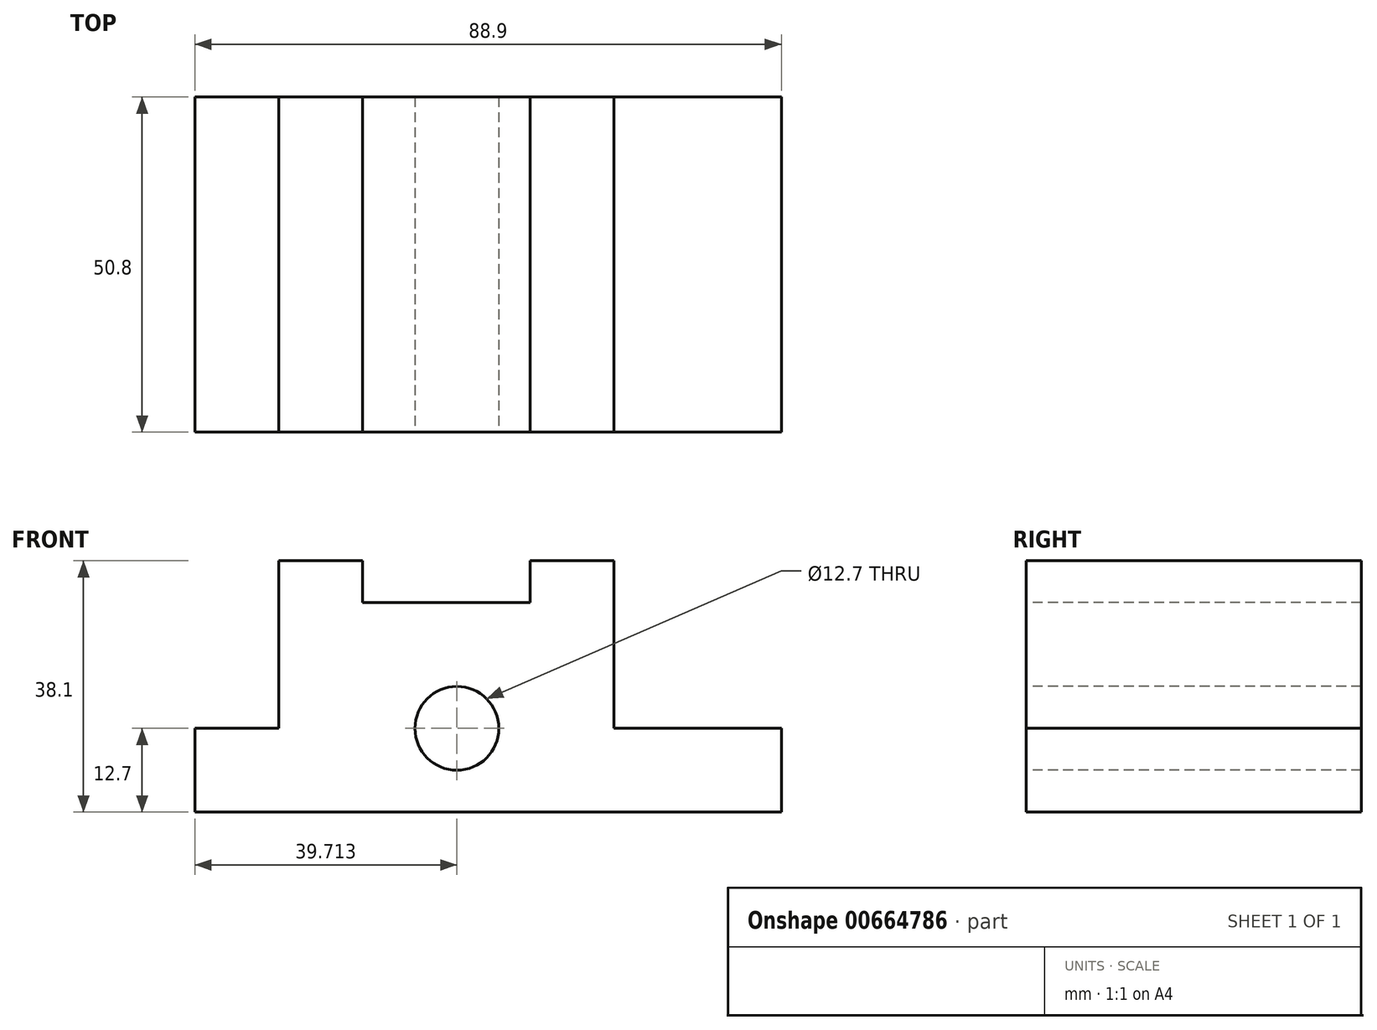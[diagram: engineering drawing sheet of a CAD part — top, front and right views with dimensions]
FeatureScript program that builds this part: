
annotation { "Feature Type Name" : "Feature", "Feature Type Description" : "" }
export const myFeature = defineFeature(function(context is Context, id is Id, definition is map)
    precondition{}
    {
        {
            var Q0;
            Q0=qCreatedBy(makeId("Front.planeOp"),FACE);
            var sketch = newSketch(context, id + "F0", { "sketchPlane" : qUnion([Q0])});
            skLineSegment(sketch, "E0.bottom", {"start": v(-44.45, 19.05) * mm, "end": v(44.45, 19.05) * mm});
            skLineSegment(sketch, "E0.top", {"start": v(-44.45, -19.05) * mm, "end": v(44.45, -19.05) * mm});
            skLineSegment(sketch, "E0.left", {"start": v(-44.45, 19.05) * mm, "end": v(-44.45, -19.05) * mm});
            skLineSegment(sketch, "E0.right", {"start": v(44.45, 19.05) * mm, "end": v(44.45, -19.05) * mm});
            skPoint(sketch, "E0.middle", {"position": v(0, 0) * mm});
            skSolve(sketch);
        }
        {
            var Q0;
            Q0=makeQuery(id+"F0.imprint","IMPRINT",FACE,{"disambiguationData":[TD([[makeQuery(id+"F0.imprint","IMPRINT",EDGE,{"derivedFrom":sQuery(id+"F0.wireOp",EDGE,"E0.bottom")}),-1.0]])]});
            extrude(context, id + "F1", {"entities" : qUnion([Q0]), "depth" : 50.8 * mm, "offsetDistance" : 25.4 * mm});
        }
        {
            var Q0;
            Q0=makeQuery(id+"F1.opExtrude","CAP_FACE",FACE,{"disambiguationData":[OSD([sQuery(id+"F0.wireOp",EDGE,"E0.bottom"),sQuery(id+"F0.wireOp",EDGE,"E0.top"),sQuery(id+"F0.wireOp",EDGE,"E0.left"),sQuery(id+"F0.wireOp",EDGE,"E0.right")])],"isStart":false});
            var sketch = newSketch(context, id + "F2", { "sketchPlane" : qUnion([Q0])});
            skLineSegment(sketch, "E1.bottom", {"start": v(-44.45, 19.05) * mm, "end": v(-31.75, 19.05) * mm});
            skLineSegment(sketch, "E1.top", {"start": v(-44.45, -6.35) * mm, "end": v(-31.75, -6.35) * mm});
            skLineSegment(sketch, "E1.left", {"start": v(-44.45, 19.05) * mm, "end": v(-44.45, -6.35) * mm});
            skLineSegment(sketch, "E1.right", {"start": v(-31.75, 19.05) * mm, "end": v(-31.75, -6.35) * mm});
            skSolve(sketch);
        }
        {
            var Q0;
            Q0=makeQuery(id+"F2.imprint","IMPRINT",FACE,{"disambiguationData":[TD([[makeQuery(id+"F2.imprint","IMPRINT",EDGE,{"derivedFrom":sQuery(id+"F2.wireOp",EDGE,"E1.bottom")}),-1.0]])]});
            extrude(context, id + "F3", {"entities" : qUnion([Q0]), "operationType" : NewBodyOperationType.REMOVE, "endBound" : BoundingType.THROUGH_ALL, "oppositeDirection" : true, "depth" : 25.4 * mm, "offsetDistance" : 25.4 * mm});
        }
        {
            var Q0;
            Q0=makeQuery(id+"F1.opExtrude","CAP_FACE",FACE,{"disambiguationData":[OSD([sQuery(id+"F0.wireOp",EDGE,"E0.bottom"),sQuery(id+"F0.wireOp",EDGE,"E0.top"),sQuery(id+"F0.wireOp",EDGE,"E0.left"),sQuery(id+"F0.wireOp",EDGE,"E0.right")])],"isStart":false});
            var sketch = newSketch(context, id + "F4", { "sketchPlane" : qUnion([Q0])});
            skLineSegment(sketch, "E2.bottom", {"start": v(44.45, 19.05) * mm, "end": v(19.05, 19.05) * mm});
            skLineSegment(sketch, "E2.top", {"start": v(44.45, -6.35) * mm, "end": v(19.05, -6.35) * mm});
            skLineSegment(sketch, "E2.left", {"start": v(44.45, 19.05) * mm, "end": v(44.45, -6.35) * mm});
            skLineSegment(sketch, "E2.right", {"start": v(19.05, 19.05) * mm, "end": v(19.05, -6.35) * mm});
            skSolve(sketch);
        }
        {
            var Q0;
            Q0=makeQuery(id+"F4.imprint","IMPRINT",FACE,{"disambiguationData":[TD([[makeQuery(id+"F4.imprint","IMPRINT",EDGE,{"derivedFrom":sQuery(id+"F4.wireOp",EDGE,"E2.bottom")}),-1.0]])]});
            extrude(context, id + "F5", {"entities" : qUnion([Q0]), "operationType" : NewBodyOperationType.REMOVE, "endBound" : BoundingType.THROUGH_ALL, "oppositeDirection" : true, "depth" : 25.4 * mm, "offsetDistance" : 25.4 * mm});
        }
        {
            var Q0;
            Q0=makeQuery(id+"F1.opExtrude","CAP_FACE",FACE,{"disambiguationData":[OSD([sQuery(id+"F0.wireOp",EDGE,"E0.bottom"),sQuery(id+"F0.wireOp",EDGE,"E0.top"),sQuery(id+"F0.wireOp",EDGE,"E0.left"),sQuery(id+"F0.wireOp",EDGE,"E0.right")])],"isStart":false});
            var sketch = newSketch(context, id + "F6", { "sketchPlane" : qUnion([Q0])});
            skCircle(sketch, "E3", {"center": v(-4.74, -6.35) * mm, "radius": 6.35 * mm});
            skSolve(sketch);
        }
        {
            var Q0;
            Q0=makeQuery(id+"F6.imprint","IMPRINT",FACE,{"disambiguationData":[TD([[makeQuery(id+"F6.imprint","IMPRINT",EDGE,{"derivedFrom":sQuery(id+"F6.wireOp",EDGE,"E3")}),1.0]])]});
            var Q1;
            Q1=sQuery(id+"F6.wireOp",EDGE,"E3");
            extrude(context, id + "F7", {"entities" : qUnion([Q0]), "operationType" : NewBodyOperationType.REMOVE, "surfaceEntities" : qUnion([Q1]), "endBound" : BoundingType.THROUGH_ALL, "oppositeDirection" : true, "depth" : 25.4 * mm, "offsetDistance" : 25.4 * mm});
        }
        {
            var Q0;
            Q0=makeQuery(id+"F1.opExtrude","SWEPT_FACE",FACE,{"disambiguationData":[OSD([sQuery(id+"F0.wireOp",EDGE,"E0.bottom")])]});
            var sketch = newSketch(context, id + "F8", { "sketchPlane" : qUnion([Q0])});
            skLineSegment(sketch, "E4.bottom", {"start": v(-19.05, 0) * mm, "end": v(6.35, 0) * mm});
            skLineSegment(sketch, "E4.top", {"start": v(-19.05, -50.8) * mm, "end": v(6.35, -50.8) * mm});
            skLineSegment(sketch, "E4.left", {"start": v(-19.05, 0) * mm, "end": v(-19.05, -50.8) * mm});
            skLineSegment(sketch, "E4.right", {"start": v(6.35, 0) * mm, "end": v(6.35, -50.8) * mm});
            skSolve(sketch);
        }
        {
            var Q0;
            Q0=makeQuery(id+"F8.imprint","IMPRINT",FACE,{"disambiguationData":[TD([[makeQuery(id+"F8.imprint","IMPRINT",EDGE,{"derivedFrom":sQuery(id+"F8.wireOp",EDGE,"E4.bottom")}),-1.0]])]});
            extrude(context, id + "F9", {"entities" : qUnion([Q0]), "operationType" : NewBodyOperationType.REMOVE, "oppositeDirection" : true, "depth" : 6.35 * mm, "offsetDistance" : 25.4 * mm});
        }
    });
